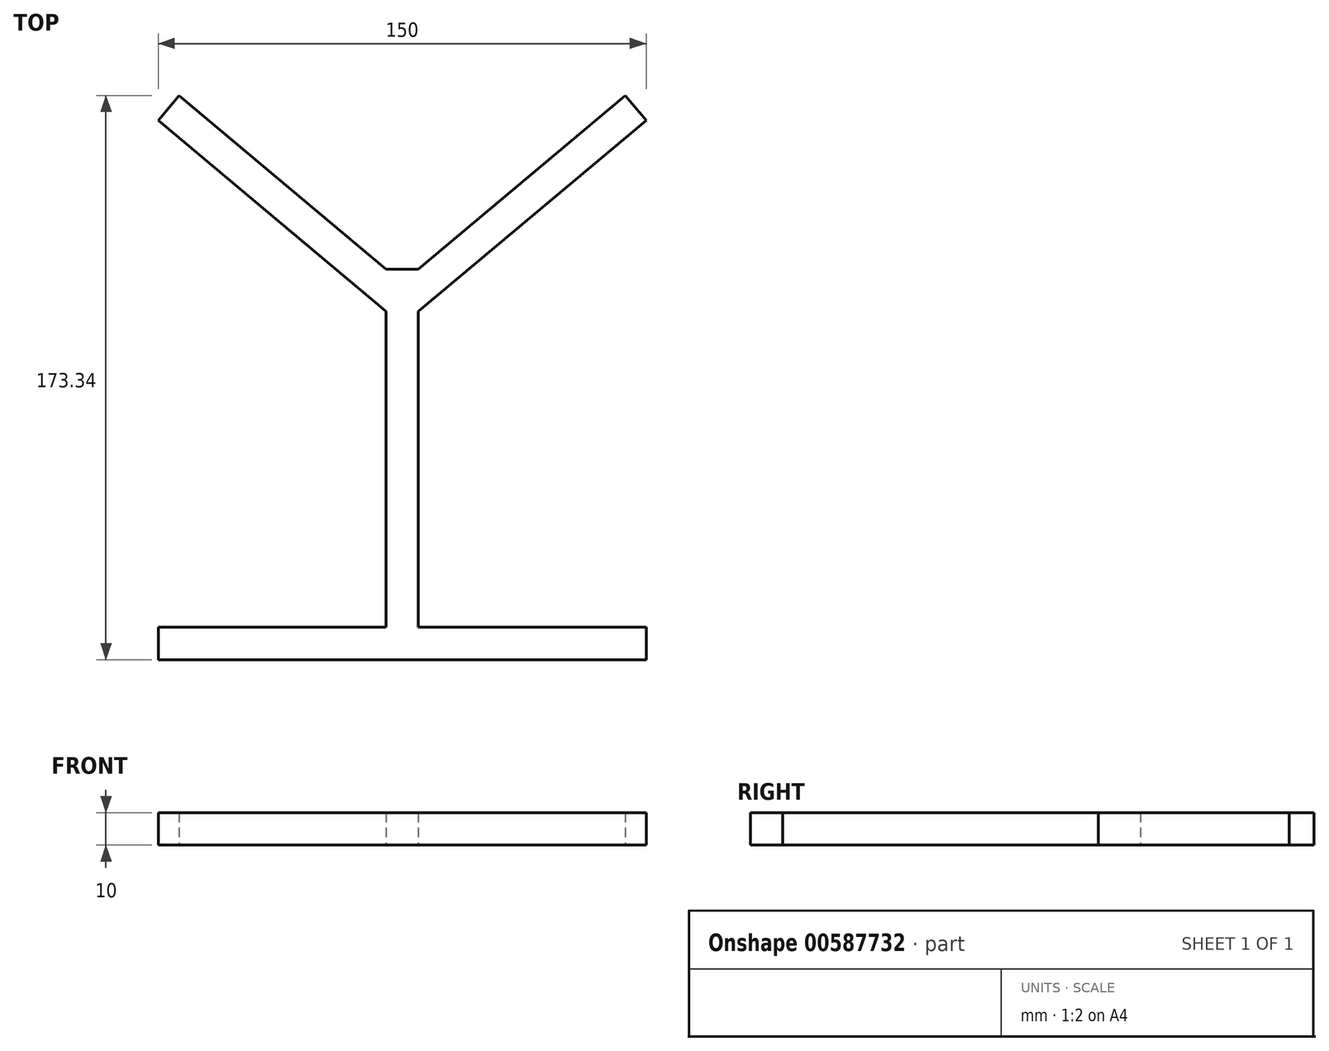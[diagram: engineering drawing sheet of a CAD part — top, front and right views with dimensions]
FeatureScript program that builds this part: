
annotation { "Feature Type Name" : "Feature", "Feature Type Description" : "" }
export const myFeature = defineFeature(function(context is Context, id is Id, definition is map)
    precondition{}
    {
        {
            var Q0;
            Q0=qCreatedBy(makeId("Top.planeOp"),FACE);
            var sketch = newSketch(context, id + "F0", { "sketchPlane" : qUnion([Q0])});
            skLineSegment(sketch, "E0.bottom", {"start": v(-5, 57.5) * mm, "end": v(5, 57.5) * mm});
            skLineSegment(sketch, "E0.left", {"start": v(-5, 44.45) * mm, "end": v(-5, -52.5) * mm});
            skLineSegment(sketch, "E0.right", {"start": v(5, 44.45) * mm, "end": v(5, -52.5) * mm});
            skPoint(sketch, "E0.middle", {"position": v(0, 0) * mm});
            skLineSegment(sketch, "E1.bottom", {"start": v(75, -52.5) * mm, "end": v(5, -52.5) * mm});
            skLineSegment(sketch, "E1.top", {"start": v(75, -62.5) * mm, "end": v(-75, -62.5) * mm});
            skLineSegment(sketch, "E1.left", {"start": v(75, -52.5) * mm, "end": v(75, -62.5) * mm});
            skLineSegment(sketch, "E1.right", {"start": v(-75, -52.5) * mm, "end": v(-75, -62.5) * mm});
            skPoint(sketch, "E1.middle", {"position": v(0, -57.5) * mm});
            skLineSegment(sketch, "E2", {"start": v(-5, 57.5) * mm, "end": v(-68.57, 110.84) * mm});
            skLineSegment(sketch, "E3", {"start": v(-68.57, 110.84) * mm, "end": v(-75, 103.18) * mm});
            skLineSegment(sketch, "E4", {"start": v(-75, 103.18) * mm, "end": v(-5, 44.45) * mm});
            skLineSegment(sketch, "E5", {"start": v(5, 57.5) * mm, "end": v(68.57, 110.84) * mm});
            skLineSegment(sketch, "E6", {"start": v(68.57, 110.84) * mm, "end": v(75, 103.18) * mm});
            skLineSegment(sketch, "E7", {"start": v(75, 103.18) * mm, "end": v(5, 44.45) * mm});
            skPoint(sketch, "E8.orphan", {"position": v(-5, -57.5) * mm});
            skPoint(sketch, "E9.orphan", {"position": v(5, -57.5) * mm});
            skLineSegment(sketch, "E10.trimOffspring", {"start": v(-5, -52.5) * mm, "end": v(-75, -52.5) * mm});
            skSolve(sketch);
        }
        {
            var Q0;
            Q0=makeQuery(id+"F0.imprint","IMPRINT",FACE,{"disambiguationData":[TD([[makeQuery(id+"F0.imprint","IMPRINT",EDGE,{"derivedFrom":sQuery(id+"F0.wireOp",EDGE,"E0.bottom")}),-1.0]])]});
            extrude(context, id + "F1", {"entities" : qUnion([Q0]), "endBound" : BoundingType.SYMMETRIC, "depth" : 10 * mm, "offsetDistance" : 25 * mm});
        }
    });
